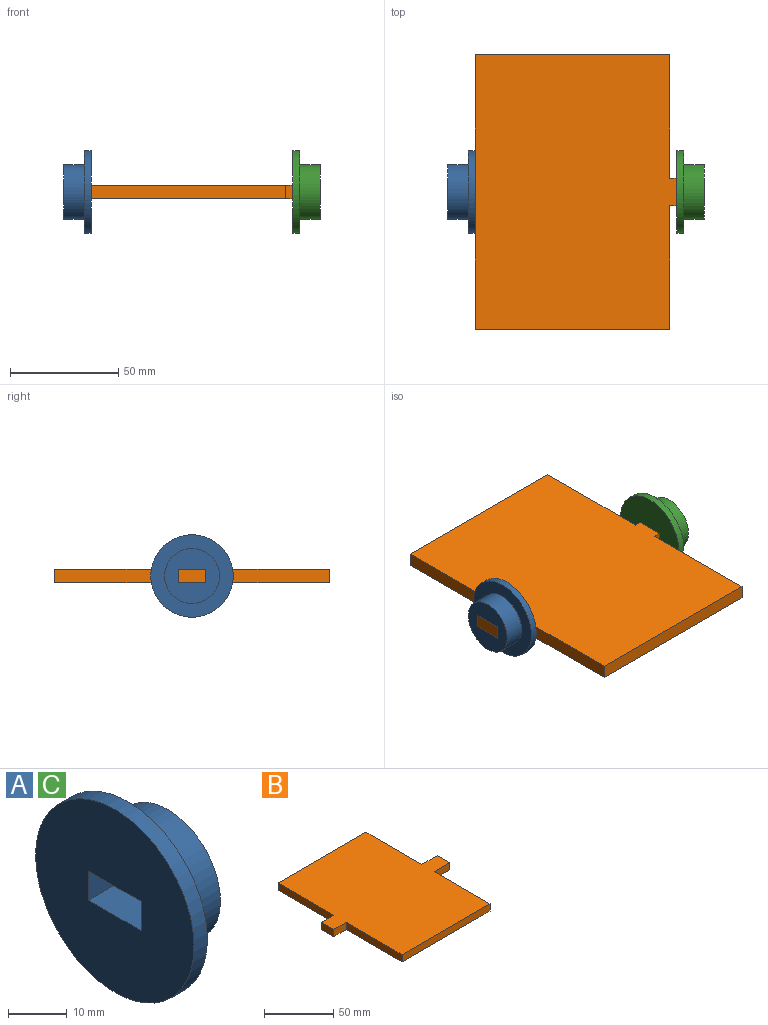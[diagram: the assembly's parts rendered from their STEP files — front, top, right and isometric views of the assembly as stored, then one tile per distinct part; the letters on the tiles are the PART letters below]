
ASSEMBLY  parts=3 mates=1
PART A: 9 faces, bbox 12.7x38.1x38.1 mm
  f0: plane 38.1x38.1mm, normal (-1,0,0), area 1062.7mm2, adj f2,f5,f6,f7,f8
  f1: plane 25.4x25.4mm, normal (1,0,0), area 429.3mm2, adj f4,f5,f6,f7,f8
  f2: cylinder r=19.05mm len=38.1mm, axis (-1,0,0), area 380mm2, adj f0,f3
  f3: plane 38.1x38.1mm, normal (1,0,0), area 633.4mm2, adj f2,f4
  f4: cylinder r=12.7mm len=25.4mm, axis (-1,0,0), area 760.1mm2, adj f1,f3
  f5: plane 12.7x6.1mm, normal (0,1,0), area 77.4mm2, adj f0,f1,f6,f8
  f6: plane 12.7x12.7mm, normal (0,0,1), area 161.3mm2, adj f0,f1,f5,f7
  f7: plane 12.7x6.1mm, normal (0,-1,0), area 77.4mm2, adj f0,f1,f6,f8
  f8: plane 12.7x12.7mm, normal (0,0,-1), area 161.3mm2, adj f0,f1,f5,f7
PART B: 14 faces, bbox 118.6x127x6.4 mm
  f0: plane 12.7x6.35mm, normal (1,0,0), area 80.6mm2, adj f1,f11,f12,f13
  f1: plane 15.88x6.35mm, normal (0,1,0), area 100.8mm2, adj f0,f2,f12,f13
  f2: plane 57.15x6.35mm, normal (1,0,0), area 362.9mm2, adj f1,f3,f12,f13
  f3: plane 90.04x6.35mm, normal (0,1,0), area 571.8mm2, adj f2,f4,f12,f13
  f4: plane 57.15x6.35mm, normal (-1,0,0), area 362.9mm2, adj f3,f5,f12,f13
  f5: plane 12.7x6.35mm, normal (0,1,0), area 80.6mm2, adj f4,f6,f12,f13
  f6: plane 12.7x6.35mm, normal (-1,0,0), area 80.6mm2, adj f5,f7,f12,f13
  f7: plane 12.7x6.35mm, normal (0,-1,0), area 80.6mm2, adj f6,f8,f12,f13
  f8: plane 57.15x6.35mm, normal (-1,0,0), area 362.9mm2, adj f7,f9,f12,f13
  f9: plane 90.04x6.35mm, normal (0,-1,0), area 571.8mm2, adj f8,f10,f12,f13
  f10: plane 57.15x6.35mm, normal (1,0,0), area 362.9mm2, adj f9,f11,f12,f13
  f11: plane 15.88x6.35mm, normal (0,-1,0), area 100.8mm2, adj f0,f10,f12,f13
  f12: plane 127x118.62mm, normal (0,0,1), area 11798.4mm2, adj f0,f1,f2,f3,f4,f5,f6,f7
  f13: plane 127x118.62mm, normal (0,0,-1), area 11798.4mm2, adj f0,f1,f2,f3,f4,f5,f6,f7
PART C: same geometry as A
PLACE A rot(axis=(0,1,0),180deg) t=(-12.7,63.5,3.18)mm
PLACE B t=(-12.7,0,0)mm
PLACE C t=(80.52,63.5,3.18)mm
MATE fastened B.f6 <-> A.f2  axis (-1,0,0) through (-25.4,63.5,3.18)mm
